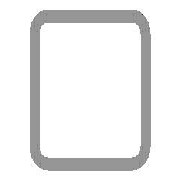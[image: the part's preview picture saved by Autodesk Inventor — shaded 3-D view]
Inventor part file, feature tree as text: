
AUTODESK INVENTOR PART (.ipt)
format: ipt  version: 2018 (Build 220112000, 112)  size: 159,232 bytes
history: native  units: mm (DEFAULTED — no unit token found)
features: sketch x5, other x3, extrude x2, hole x1, plane x1
ambient origin geometry x8: Origin, YZ Plane, XZ Plane, XY Plane, X Axis, Y Axis, Z Axis, Center Point
bodies: Solid1 (feature_tree)
feature tree (12):
  other  "Driven Length"
  other  "Piano iniziale"
  other  "Piano finale"
  extrude  "Corpo"  TaperAngle=0.0deg  [1 undecoded]
  extrude  "Estrusione2"  Depth=20.0mm
  hole  "Foro1"  [1 undecoded]
  sketch  "Schizzo"
  sketch  "Sketch3"  dims[d3=200.0mm d4=0.0mm]
  plane  "Work Plane3"
  sketch  "Sketch4"  dims[d7=4.0mm d9=20.0mm d11=20.0mm d12=2.0mm d13=-0.0mm d14=200.0mm d15=10.0mm d16=10.0mm d17=90.0deg d18=200.0mm d19=45.0deg d20=45.0deg d21=10.0mm d22=0.0mm d23=8.0mm d24=6.0mm d25=4.0mm d26=2.0mm d27=90.0deg d28=8.0mm d29=20.594885mm]
  sketch  "Schizzo5"
  sketch  "Schizzo6"
note: 2 required parameter values undecoded (feature->parameter linkage not recoverable at this tier; creation-order binding heuristic only, values carry confidence <= 0.55)
